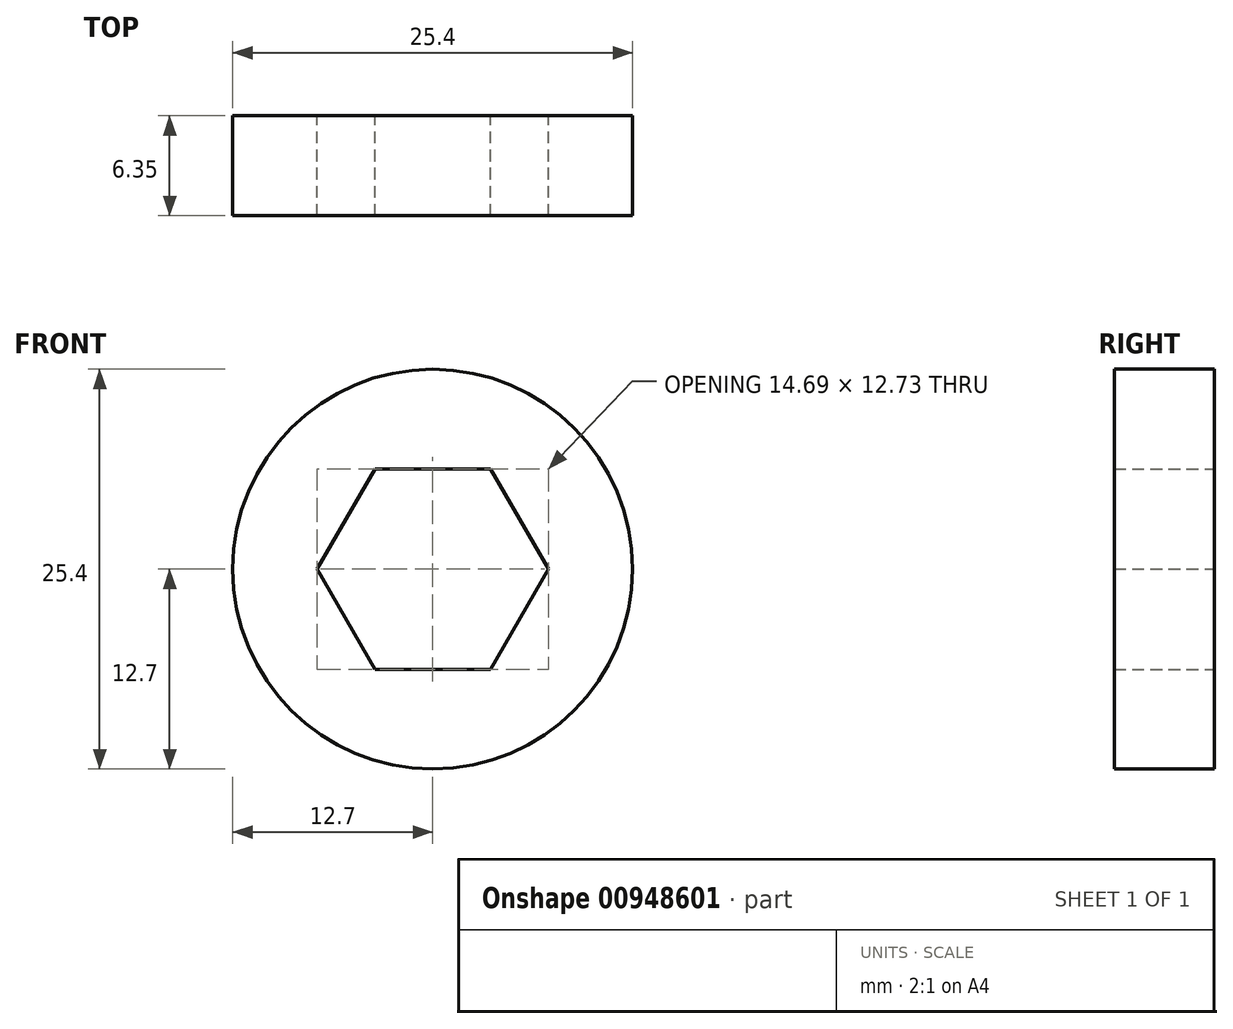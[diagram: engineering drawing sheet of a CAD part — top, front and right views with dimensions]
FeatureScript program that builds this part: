
annotation { "Feature Type Name" : "Feature", "Feature Type Description" : "" }
export const myFeature = defineFeature(function(context is Context, id is Id, definition is map)
    precondition{}
    {
        {
            var Q0;
            Q0=qCreatedBy(makeId("Front.planeOp"),FACE);
            var sketch = newSketch(context, id + "F0", { "sketchPlane" : qUnion([Q0])});
            skCircle(sketch, "E0", {"center": v(0, 0) * mm, "radius": 12.7 * mm});
            skCircle(sketch, "E1.cCircle", {"center": v(0, 0) * mm, "radius": 6.36 * mm, "construction": true});
            skLineSegment(sketch, "E1.0", {"start": v(-3.67, 6.36) * mm, "end": v(3.67, 6.36) * mm});
            skLineSegment(sketch, "E1.1", {"start": v(3.67, 6.36) * mm, "end": v(7.35, 0) * mm});
            skLineSegment(sketch, "E1.2", {"start": v(7.35, 0) * mm, "end": v(3.67, -6.36) * mm});
            skLineSegment(sketch, "E1.3", {"start": v(3.67, -6.36) * mm, "end": v(-3.67, -6.36) * mm});
            skLineSegment(sketch, "E1.4", {"start": v(-3.67, -6.36) * mm, "end": v(-7.35, 0) * mm});
            skLineSegment(sketch, "E1.5", {"start": v(-7.35, 0) * mm, "end": v(-3.67, 6.36) * mm});
            skPoint(sketch, "E1.0.midPoint", {"position": v(0, 6.36) * mm});
            skSolve(sketch);
        }
        {
            var Q0;
            Q0 = qSketchRegion(id + "F0", true);
            extrude(context, id + "F1", {"entities" : qUnion([Q0]), "depth" : 6.35 * mm, "offsetDistance" : 25.4 * mm});
        }
    });
